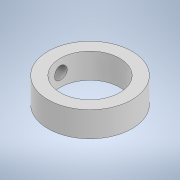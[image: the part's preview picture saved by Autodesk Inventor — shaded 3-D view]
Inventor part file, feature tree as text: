
AUTODESK INVENTOR PART (.ipt)
format: ipt  version: 2021 (Build 250183000, 183)  size: 110,080 bytes
history: native  units: mm
features: extrude x2, sketch x2
ambient origin geometry x8: Origin, YZ Plane, XZ Plane, XY Plane, X Axis, Y Axis, Z Axis, Center Point
bodies: Solid1 (feature_tree)
feature tree (4):
  extrude  "Extrusion1"  Depth=20.0mm
  extrude  "Extrusion2"  Depth=3.0mm
  sketch  "Sketch1"  dims[d0=14.2mm d1=20.0mm]
  sketch  "Sketch2"  dims[d2=6.0mm d3=0.0mm d4=3.0mm d5=3.0mm d6=0.0mm d7=0.0mm]
